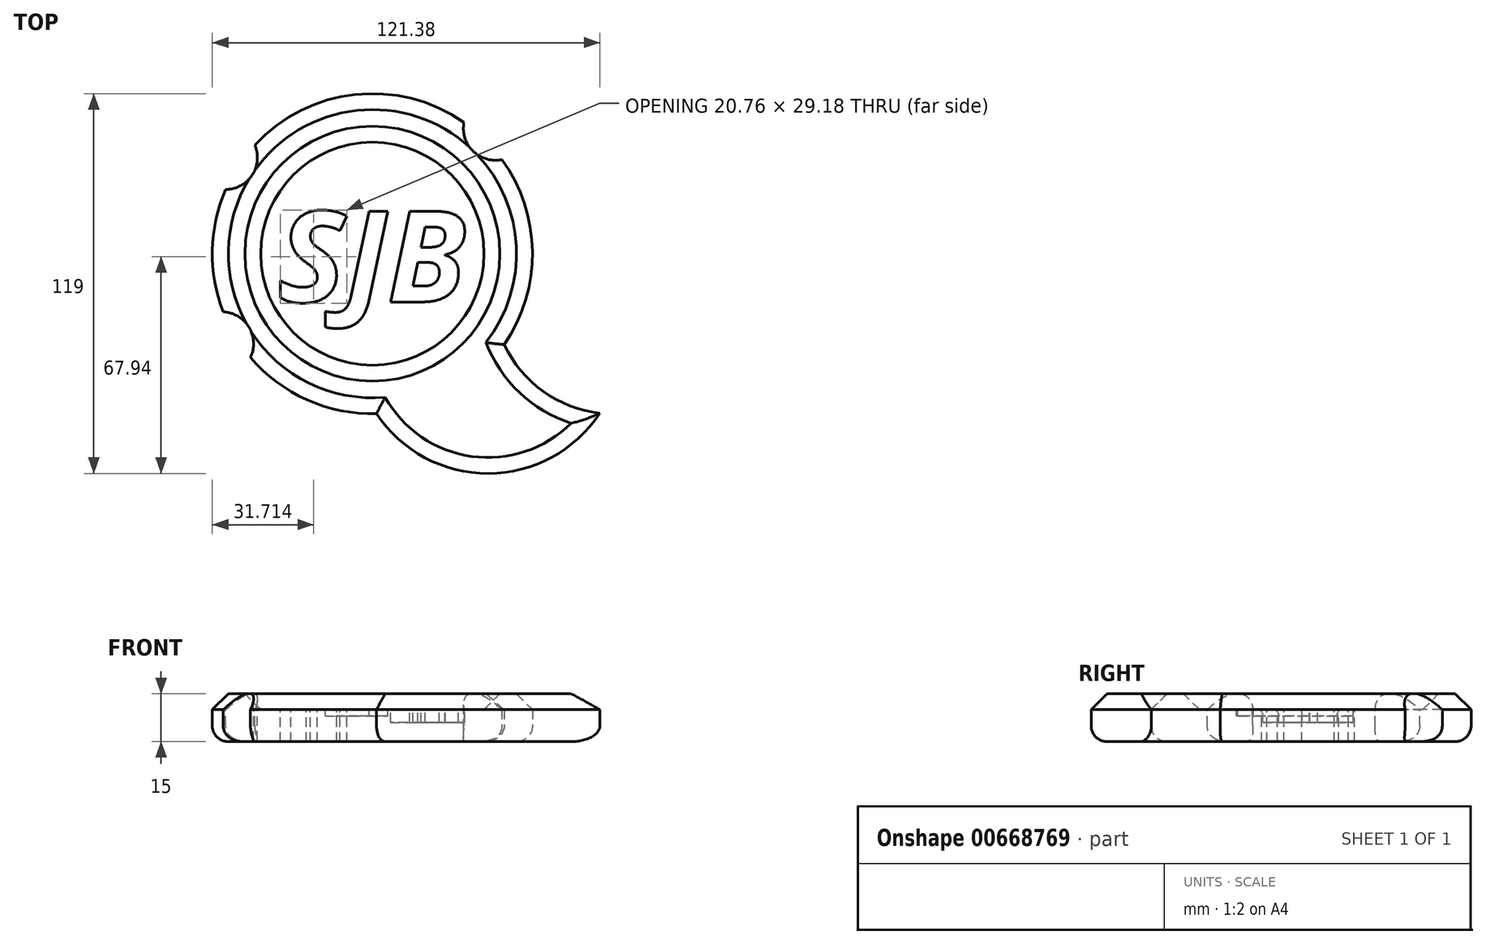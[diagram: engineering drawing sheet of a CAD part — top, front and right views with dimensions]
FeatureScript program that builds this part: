
annotation { "Feature Type Name" : "Feature", "Feature Type Description" : "" }
export const myFeature = defineFeature(function(context is Context, id is Id, definition is map)
    precondition{}
    {
        {
            var Q0;
            Q0=qCreatedBy(makeId("Top.planeOp"),FACE);
            var sketch = newSketch(context, id + "F0", { "sketchPlane" : qUnion([Q0])});
            skCircle(sketch, "E0", {"center": v(0, 0) * mm, "radius": 50.14 * mm});
            skSolve(sketch);
        }
        {
            var Q0;
            Q0=makeQuery(id+"F0.imprint","IMPRINT",FACE,{"disambiguationData":[TD([[makeQuery(id+"F0.imprint","IMPRINT",EDGE,{"derivedFrom":sQuery(id+"F0.wireOp",EDGE,"E0")}),1.0]])]});
            extrude(context, id + "F1", {"entities" : qUnion([Q0]), "depth" : 15 * mm, "offsetDistance" : 25 * mm});
        }
        {
            var Q0;
            Q0=qCreatedBy(makeId("Top.planeOp"),FACE);
            var sketch = newSketch(context, id + "F2", { "sketchPlane" : qUnion([Q0])});
            skCircle(sketch, "E1", {"center": v(36.22, -26.93) * mm, "radius": 41.93 * mm});
            skCircle(sketch, "E2", {"center": v(75.54, -12.37) * mm, "radius": 37.86 * mm});
            skSolve(sketch);
        }
        {
            var Q0;
            {var subQ0=sQuery(id+"F2.wireOp",EDGE,"E2");var subQ1=sQuery(id+"F2.wireOp",EDGE,"E1");var subQ2=makeQuery(id+"F2.imprint","INTERSECT",VERTEX,{"disambiguationData":[OD(0.0)],"derivedFrom":[subQ1,subQ0]});Q0=makeQuery(id+"F2.imprint","IMPRINT",FACE,{"disambiguationData":[TD([[makeQuery(id+"F2.imprint","IMPRINT",EDGE,{"disambiguationData":[TD([[subQ2,1.0]])],"derivedFrom":subQ1}),1.0]])]});}
            extrude(context, id + "F3", {"entities" : qUnion([Q0]), "operationType" : NewBodyOperationType.ADD, "depth" : 15 * mm, "offsetDistance" : 25 * mm});
        }
        {
            var Q0;
            Q0=makeQuery(id+"F3.boolean.opBoolean","MERGE",FACE,{"derivedFrom":[makeQuery(id+"F1.opExtrude","CAP_FACE",FACE,{"disambiguationData":[OSD([sQuery(id+"F0.wireOp",EDGE,"E0")])],"isStart":false}),makeQuery(id+"F3.opExtrude","CAP_FACE",FACE,{"disambiguationData":[OSD([sQuery(id+"F2.wireOp",EDGE,"E1"),sQuery(id+"F2.wireOp",EDGE,"E2")])],"isStart":false})]});
            var sketch = newSketch(context, id + "F4", { "sketchPlane" : qUnion([Q0])});
            skCircle(sketch, "E3", {"center": v(0, 0) * mm, "radius": 39.94 * mm});
            skSolve(sketch);
        }
        {
            var Q0;
            Q0=makeQuery(id+"F4.imprint","IMPRINT",FACE,{"disambiguationData":[TD([[makeQuery(id+"F4.imprint","IMPRINT",EDGE,{"derivedFrom":sQuery(id+"F4.wireOp",EDGE,"E3")}),1.0]])]});
            extrude(context, id + "F5", {"entities" : qUnion([Q0]), "operationType" : NewBodyOperationType.REMOVE, "oppositeDirection" : true, "depth" : 5 * mm, "offsetDistance" : 25 * mm});
        }
        {
            var Q0;
            Q0=makeQuery(id+"F3.boolean.opBoolean","MERGE",FACE,{"derivedFrom":[makeQuery(id+"F1.opExtrude","CAP_FACE",FACE,{"disambiguationData":[OSD([sQuery(id+"F0.wireOp",EDGE,"E0")])],"isStart":true}),makeQuery(id+"F3.opExtrude","CAP_FACE",FACE,{"disambiguationData":[OSD([sQuery(id+"F2.wireOp",EDGE,"E1"),sQuery(id+"F2.wireOp",EDGE,"E2")])],"isStart":true})]});
            var sketch = newSketch(context, id + "F6", { "sketchPlane" : qUnion([Q0])});
            skArc(sketch, "E4", {"start": v(1.29, 50.13) * mm, "mid": v(23.88, 44.1) * mm, "end": v(41.28, 28.47) * mm});
            skSolve(sketch);
        }
        {
            var Q0;
            Q0=makeQuery(id+"F5.boolean.opBoolean","COPY",EDGE,{"derivedFrom":makeQuery(id+"F5.opExtrude","CAP_EDGE",EDGE,{"disambiguationData":[OSD([sQuery(id+"F4.wireOp",EDGE,"E3")])],"isStart":false})});
            chamfer(context, id + "F7", {"entities" : qUnion([Q0]), "width" : 5 * mm, "tangentPropagation" : true});
        }
        {
            var Q0;
            Q0=makeQuery(id+"F1.opExtrude","CAP_EDGE",EDGE,{"disambiguationData":[OSD([sQuery(id+"F0.wireOp",EDGE,"E0")])],"isStart":false});
            chamfer(context, id + "F8", {"entities" : qUnion([Q0]), "width" : 5 * mm, "tangentPropagation" : true});
        }
        {
            var Q0;
            Q0=makeQuery(id+"F3.opExtrude","CAP_EDGE",EDGE,{"disambiguationData":[OSD([sQuery(id+"F2.wireOp",EDGE,"E1")])],"isStart":false});
            chamfer(context, id + "F9", {"entities" : qUnion([Q0]), "width" : 5 * mm, "tangentPropagation" : true});
        }
        {
            var Q0;
            Q0=makeQuery(id+"F3.opExtrude","CAP_EDGE",EDGE,{"disambiguationData":[OSD([sQuery(id+"F2.wireOp",EDGE,"E2")])],"isStart":false});
            chamfer(context, id + "F10", {"entities" : qUnion([Q0]), "width" : 5 * mm, "tangentPropagation" : true});
        }
        {
            var Q0;
            Q0=makeQuery(id+"F5.boolean.opBoolean","COPY",FACE,{"derivedFrom":makeQuery(id+"F5.opExtrude","CAP_FACE",FACE,{"disambiguationData":[OSD([sQuery(id+"F4.wireOp",EDGE,"E3")])],"isStart":false})});
            var sketch = newSketch(context, id + "F11", { "sketchPlane" : qUnion([Q0])});
            skText(sketch, "E5", { "text": "SJB", "fontName": "OpenSans-BoldItalic.ttf"});
            const initialGuessF11  = {"E5": [-0.0296, -0.01512, 1, 0, 0.02863]};
            skSetInitialGuess(sketch, initialGuessF11);
            skSolve(sketch);
        }
        {
            var Q0;
            Q0=makeQuery(id+"F11.imprint","IMPRINT",FACE,{"disambiguationData":[TD([[makeQuery(id+"F11.imprint","IMPRINT",EDGE,{"derivedFrom":sQuery(id+"F11.wireOp",EDGE,"E5.sketch_text.stroke-34")}),-1.0]])]});
            extrude(context, id + "F12", {"entities" : qUnion([Q0]), "operationType" : NewBodyOperationType.REMOVE, "oppositeDirection" : true, "depth" : 4 * mm, "offsetDistance" : 25 * mm});
        }
        {
            var Q0;
            Q0=makeQuery(id+"F11.imprint","IMPRINT",FACE,{"disambiguationData":[TD([[makeQuery(id+"F11.imprint","IMPRINT",EDGE,{"derivedFrom":sQuery(id+"F11.wireOp",EDGE,"E5.sketch_text.stroke-24")}),-1.0]])]});
            extrude(context, id + "F13", {"entities" : qUnion([Q0]), "operationType" : NewBodyOperationType.REMOVE, "oppositeDirection" : true, "depth" : 2 * mm, "offsetDistance" : 25 * mm});
        }
        {
            var Q0;
            Q0=makeQuery(id+"F11.imprint","IMPRINT",FACE,{"disambiguationData":[TD([[makeQuery(id+"F11.imprint","IMPRINT",EDGE,{"derivedFrom":sQuery(id+"F11.wireOp",EDGE,"E5.sketch_text.stroke-0")}),-1.0]])]});
            extrude(context, id + "F14", {"entities" : qUnion([Q0]), "operationType" : NewBodyOperationType.REMOVE, "endBound" : BoundingType.THROUGH_ALL, "oppositeDirection" : true, "depth" : 2 * mm, "offsetDistance" : 25 * mm});
        }
        {
            var Q0;
            Q0=qCreatedBy(makeId("Top.planeOp"),FACE);
            var sketch = newSketch(context, id + "F15", { "sketchPlane" : qUnion([Q0])});
            skCircle(sketch, "E6", {"center": v(38.5, 39.28) * mm, "radius": 10 * mm});
            skSolve(sketch);
        }
        {
            var Q0;
            Q0=makeQuery(id+"F15.imprint","IMPRINT",FACE,{"disambiguationData":[TD([[makeQuery(id+"F15.imprint","IMPRINT",EDGE,{"derivedFrom":sQuery(id+"F15.wireOp",EDGE,"E6")}),1.0]])]});
            var Q1;
            Q1=sQuery(id+"F15.wireOp",EDGE,"E6");
            extrude(context, id + "F16", {"entities" : qUnion([Q0]), "operationType" : NewBodyOperationType.REMOVE, "surfaceEntities" : qUnion([Q1]), "depth" : 25 * mm, "offsetDistance" : 25 * mm});
        }
        {
            var Q0;
            Q0=makeQuery(id+"F4.imprint","IMPRINT",FACE,{"disambiguationData":[TD([[makeQuery(id+"F4.imprint","IMPRINT",EDGE,{"derivedFrom":sQuery(id+"F4.wireOp",EDGE,"E3")}),-1.0]])]});
            var sketch = newSketch(context, id + "F17", { "sketchPlane" : qUnion([Q0])});
            skCircle(sketch, "E7", {"center": v(-46.02, 30.11) * mm, "radius": 10 * mm});
            skSolve(sketch);
        }
        {
            var Q0;
            {var subQ0=sQuery(id+"F17.wireOp",EDGE,"E7");var subQ1=makeQuery(id+"F4.imprint","IMPRINT",EDGE,{"derivedFrom":makeQuery(id+"F1.opExtrude","CAP_EDGE",EDGE,{"disambiguationData":[OSD([sQuery(id+"F0.wireOp",EDGE,"E0")])],"isStart":false})});var subQ2=makeQuery(id+"F17.imprint","INTERSECT",VERTEX,{"disambiguationData":[OD(0.0)],"derivedFrom":[subQ1,subQ0]});Q0=makeQuery(id+"F17.imprint","IMPRINT",FACE,{"disambiguationData":[TD([[makeQuery(id+"F17.imprint","IMPRINT",EDGE,{"disambiguationData":[TD([[subQ2,-1.0]])],"derivedFrom":subQ0}),1.0]])]});}
            var Q1;
            Q1=sQuery(id+"F17.wireOp",EDGE,"E7");
            extrude(context, id + "F18", {"entities" : qUnion([Q0]), "operationType" : NewBodyOperationType.REMOVE, "surfaceEntities" : qUnion([Q1]), "endBound" : BoundingType.THROUGH_ALL, "oppositeDirection" : true, "depth" : 25 * mm, "offsetDistance" : 25 * mm});
        }
        {
            var Q0;
            Q0=makeQuery(id+"F4.imprint","IMPRINT",FACE,{"disambiguationData":[TD([[makeQuery(id+"F4.imprint","IMPRINT",EDGE,{"derivedFrom":sQuery(id+"F4.wireOp",EDGE,"E3")}),-1.0]])]});
            var sketch = newSketch(context, id + "F19", { "sketchPlane" : qUnion([Q0])});
            skCircle(sketch, "E8", {"center": v(-47.22, -28.2) * mm, "radius": 10 * mm});
            skSolve(sketch);
        }
        {
            var Q0;
            {var subQ0=sQuery(id+"F19.wireOp",EDGE,"E8");var subQ1=makeQuery(id+"F4.imprint","IMPRINT",EDGE,{"derivedFrom":makeQuery(id+"F1.opExtrude","CAP_EDGE",EDGE,{"disambiguationData":[OSD([sQuery(id+"F0.wireOp",EDGE,"E0")])],"isStart":false})});var subQ2=makeQuery(id+"F19.imprint","INTERSECT",VERTEX,{"disambiguationData":[OD(0.0)],"derivedFrom":[subQ1,subQ0]});Q0=makeQuery(id+"F19.imprint","IMPRINT",FACE,{"disambiguationData":[TD([[makeQuery(id+"F19.imprint","IMPRINT",EDGE,{"disambiguationData":[TD([[subQ2,1.0]])],"derivedFrom":subQ0}),1.0]])]});}
            var Q1;
            {var subQ0=sQuery(id+"F19.wireOp",EDGE,"E8");var subQ1=makeQuery(id+"F4.imprint","IMPRINT",EDGE,{"derivedFrom":makeQuery(id+"F1.opExtrude","CAP_EDGE",EDGE,{"disambiguationData":[OSD([sQuery(id+"F0.wireOp",EDGE,"E0")])],"isStart":false})});var subQ2=makeQuery(id+"F19.imprint","INTERSECT",VERTEX,{"disambiguationData":[OD(0.0)],"derivedFrom":[subQ1,subQ0]});Q1=makeQuery(id+"F19.imprint","IMPRINT",FACE,{"disambiguationData":[TD([[makeQuery(id+"F19.imprint","IMPRINT",EDGE,{"disambiguationData":[TD([[subQ2,-1.0]])],"derivedFrom":subQ0}),1.0]])]});}
            extrude(context, id + "F20", {"entities" : qUnion([Q0, Q1]), "operationType" : NewBodyOperationType.REMOVE, "oppositeDirection" : true, "depth" : 25 * mm, "offsetDistance" : 25 * mm});
        }
        {
            var Q0;
            Q0=makeQuery(id+"F3.opExtrude","CAP_EDGE",EDGE,{"disambiguationData":[OSD([sQuery(id+"F2.wireOp",EDGE,"E2")])],"isStart":true});
            var Q1;
            Q1=makeQuery(id+"F3.opExtrude","CAP_EDGE",EDGE,{"disambiguationData":[OSD([sQuery(id+"F2.wireOp",EDGE,"E1")])],"isStart":true});
            var Q2;
            {var subQ0=sQuery(id+"F2.wireOp",EDGE,"E2");var subQ1=sQuery(id+"F0.wireOp",EDGE,"E0");Q2=makeQuery(id+"F16.boolean.opBoolean","SPLIT",EDGE,{"disambiguationData":[TD([makeQuery(id+"F3.opExtrude","SWEPT_FACE",FACE,{"disambiguationData":[OSD([subQ0])]})])],"derivedFrom":makeQuery(id+"F1.opExtrude","CAP_EDGE",EDGE,{"disambiguationData":[OSD([subQ1])],"isStart":true})});}
            var Q3;
            {var subQ0=makeQuery(id+"F16.opExtrude","SWEPT_FACE",FACE,{"disambiguationData":[OSD([sQuery(id+"F15.wireOp",EDGE,"E6")])]});var subQ1=sQuery(id+"F2.wireOp",EDGE,"E1");var subQ3=sQuery(id+"F0.wireOp",EDGE,"E0");Q3=makeQuery(id+"F18.boolean.opBoolean","SPLIT",EDGE,{"disambiguationData":[TD([makeQuery(id+"F16.boolean.opBoolean","COPY",FACE,{"derivedFrom":subQ0})])],"derivedFrom":makeQuery(id+"F16.boolean.opBoolean","SPLIT",EDGE,{"disambiguationData":[TD([makeQuery(id+"F3.opExtrude","SWEPT_FACE",FACE,{"disambiguationData":[OSD([subQ1])]})])],"derivedFrom":makeQuery(id+"F1.opExtrude","CAP_EDGE",EDGE,{"disambiguationData":[OSD([subQ3])],"isStart":true})})});}
            var Q4;
            {var subQ0=sQuery(id+"F2.wireOp",EDGE,"E1");var subQ2=makeQuery(id+"F18.opExtrude","SWEPT_FACE",FACE,{"disambiguationData":[OSD([sQuery(id+"F17.wireOp",EDGE,"E7")])]});var subQ3=sQuery(id+"F0.wireOp",EDGE,"E0");var subQ6=makeQuery(id+"F3.opExtrude","SWEPT_FACE",FACE,{"disambiguationData":[OSD([subQ0])]});Q4=makeQuery(id+"F20.boolean.opBoolean","SPLIT",EDGE,{"disambiguationData":[TD([makeQuery(id+"F18.boolean.opBoolean","COPY",FACE,{"derivedFrom":subQ2})])],"derivedFrom":makeQuery(id+"F18.boolean.opBoolean","SPLIT",EDGE,{"disambiguationData":[TD([subQ6])],"derivedFrom":makeQuery(id+"F16.boolean.opBoolean","SPLIT",EDGE,{"disambiguationData":[TD([subQ6])],"derivedFrom":makeQuery(id+"F1.opExtrude","CAP_EDGE",EDGE,{"disambiguationData":[OSD([subQ3])],"isStart":true})})})});}
            var Q5;
            {var subQ0=sQuery(id+"F2.wireOp",EDGE,"E1");var subQ2=makeQuery(id+"F3.opExtrude","SWEPT_FACE",FACE,{"disambiguationData":[OSD([subQ0])]});var subQ3=sQuery(id+"F0.wireOp",EDGE,"E0");Q5=makeQuery(id+"F20.boolean.opBoolean","SPLIT",EDGE,{"disambiguationData":[TD([subQ2])],"derivedFrom":makeQuery(id+"F18.boolean.opBoolean","SPLIT",EDGE,{"disambiguationData":[TD([subQ2])],"derivedFrom":makeQuery(id+"F16.boolean.opBoolean","SPLIT",EDGE,{"disambiguationData":[TD([subQ2])],"derivedFrom":makeQuery(id+"F1.opExtrude","CAP_EDGE",EDGE,{"disambiguationData":[OSD([subQ3])],"isStart":true})})})});}
            fillet(context, id + "F21", {"entities" : qUnion([Q0, Q1, Q2, Q3, Q4, Q5]), "radius" : 5 * mm, "tangentPropagation" : true, "allowEdgeOverflow" : false});
        }
    });
